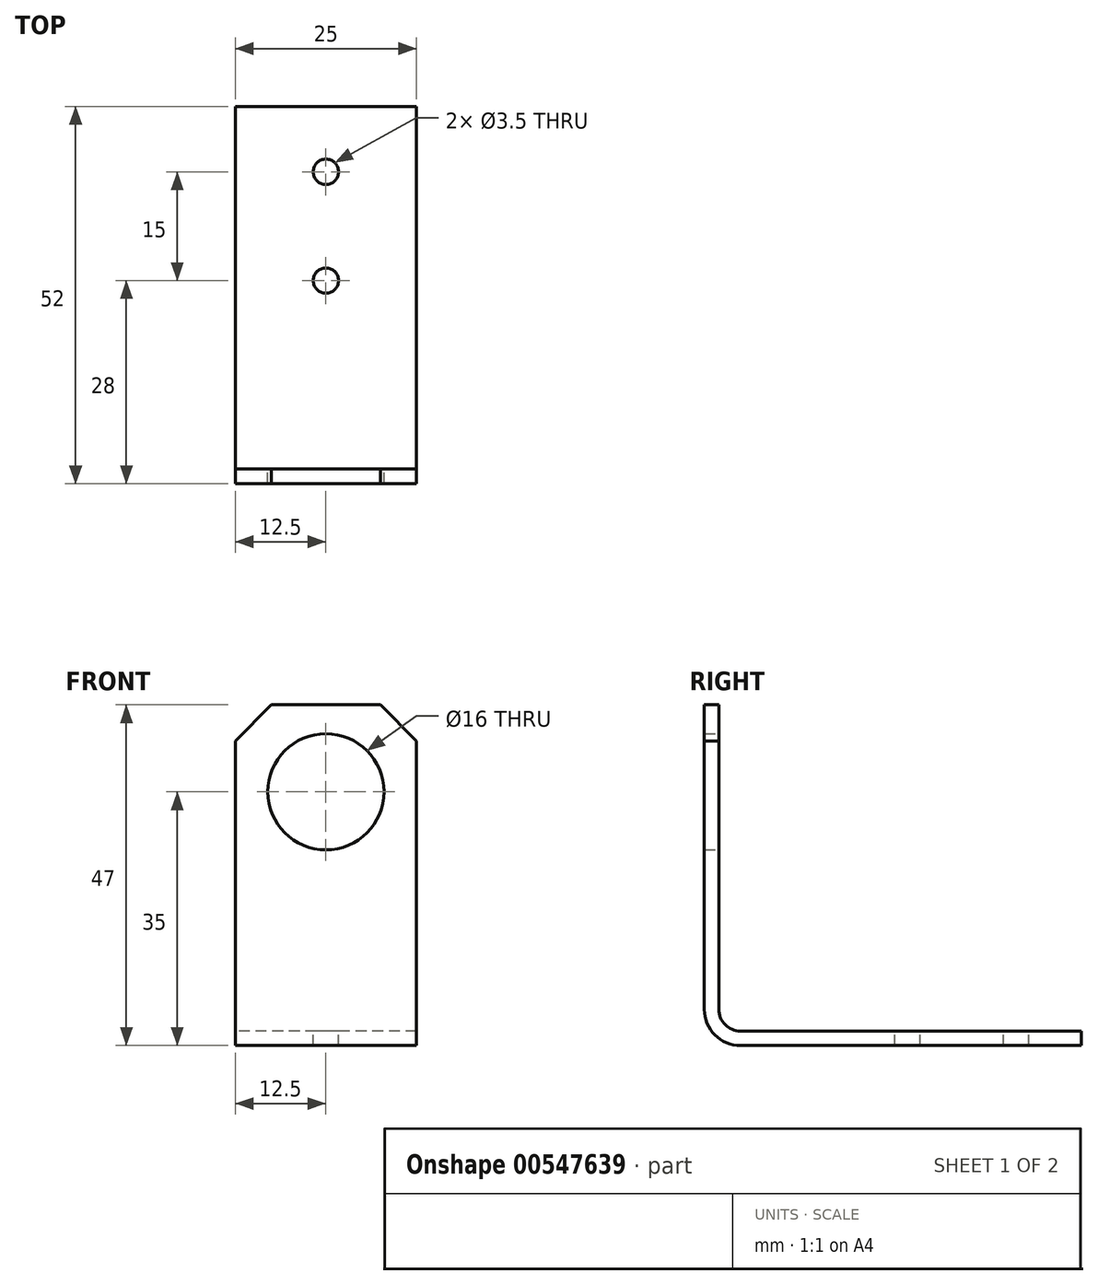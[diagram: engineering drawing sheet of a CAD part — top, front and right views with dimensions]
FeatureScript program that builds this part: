
annotation { "Feature Type Name" : "Feature", "Feature Type Description" : "" }
export const myFeature = defineFeature(function(context is Context, id is Id, definition is map)
    precondition{}
    {
        {
            var Q0;
            Q0=qCreatedBy(makeId("Right.planeOp"),FACE);
            var sketch = newSketch(context, id + "F0", { "sketchPlane" : qUnion([Q0])});
            skLineSegment(sketch, "E0", {"start": v(0, 47) * mm, "end": v(0, 5) * mm});
            skLineSegment(sketch, "E1", {"start": v(5, 0) * mm, "end": v(52, 0) * mm});
            skPoint(sketch, "E2.visualSharp", {"position": v(0, 0) * mm});
            skArc(sketch, "E2.filletArc", {"start": v(0, 5) * mm, "mid": v(1.46, 1.46) * mm, "end": v(5, 0) * mm});
            skLineSegment(sketch, "E3.0", {"start": v(5, 2) * mm, "end": v(52, 2) * mm});
            skArc(sketch, "E3.1", {"start": v(2, 5) * mm, "mid": v(2.88, 2.88) * mm, "end": v(5, 2) * mm});
            skLineSegment(sketch, "E3.2", {"start": v(2, 47) * mm, "end": v(2, 5) * mm});
            skLineSegment(sketch, "E4", {"start": v(52, 2) * mm, "end": v(52, 0) * mm});
            skLineSegment(sketch, "E5", {"start": v(0, 47) * mm, "end": v(2, 47) * mm});
            skSolve(sketch);
        }
        {
            var Q0;
            Q0=makeQuery(id+"F0.imprint","IMPRINT",FACE,{"disambiguationData":[TD([[makeQuery(id+"F0.imprint","IMPRINT",EDGE,{"derivedFrom":sQuery(id+"F0.wireOp",EDGE,"E0")}),1.0]])]});
            extrude(context, id + "F1", {"entities" : qUnion([Q0]), "depth" : 25 * mm, "offsetDistance" : 25 * mm});
        }
        {
            var Q0;
            Q0=makeQuery(id+"F1.opExtrude","SWEPT_FACE",FACE,{"disambiguationData":[OSD([sQuery(id+"F0.wireOp",EDGE,"E3.2")])]});
            var sketch = newSketch(context, id + "F2", { "sketchPlane" : qUnion([Q0])});
            skCircle(sketch, "E6", {"center": v(-12.5, 35) * mm, "radius": 8 * mm});
            skSolve(sketch);
        }
        {
            var Q0;
            Q0 = qSketchRegion(id + "F2", true);
            extrude(context, id + "F3", {"entities" : qUnion([Q0]), "operationType" : NewBodyOperationType.REMOVE, "oppositeDirection" : true, "depth" : 25 * mm, "offsetDistance" : 25 * mm});
        }
        {
            var Q0;
            Q0=makeQuery(id+"F1.opExtrude","CAP_EDGE",EDGE,{"disambiguationData":[OSD([sQuery(id+"F0.wireOp",EDGE,"E5")])],"isStart":true});
            var Q1;
            Q1=makeQuery(id+"F1.opExtrude","CAP_EDGE",EDGE,{"disambiguationData":[OSD([sQuery(id+"F0.wireOp",EDGE,"E5")])],"isStart":false});
            chamfer(context, id + "F4", {"entities" : qUnion([Q0, Q1]), "width" : 5 * mm, "tangentPropagation" : true});
        }
        {
            var Q0;
            Q0=makeQuery(id+"F1.opExtrude","SWEPT_FACE",FACE,{"disambiguationData":[OSD([sQuery(id+"F0.wireOp",EDGE,"E3.0")])]});
            var sketch = newSketch(context, id + "F5", { "sketchPlane" : qUnion([Q0])});
            skCircle(sketch, "E7", {"center": v(12.5, 43) * mm, "radius": 1.75 * mm});
            skCircle(sketch, "E8", {"center": v(12.5, 28) * mm, "radius": 1.75 * mm});
            skSolve(sketch);
        }
        {
            var Q0;
            Q0 = qSketchRegion(id + "F5", true);
            extrude(context, id + "F6", {"entities" : qUnion([Q0]), "operationType" : NewBodyOperationType.REMOVE, "oppositeDirection" : true, "depth" : 25 * mm, "offsetDistance" : 25 * mm});
        }
    });
